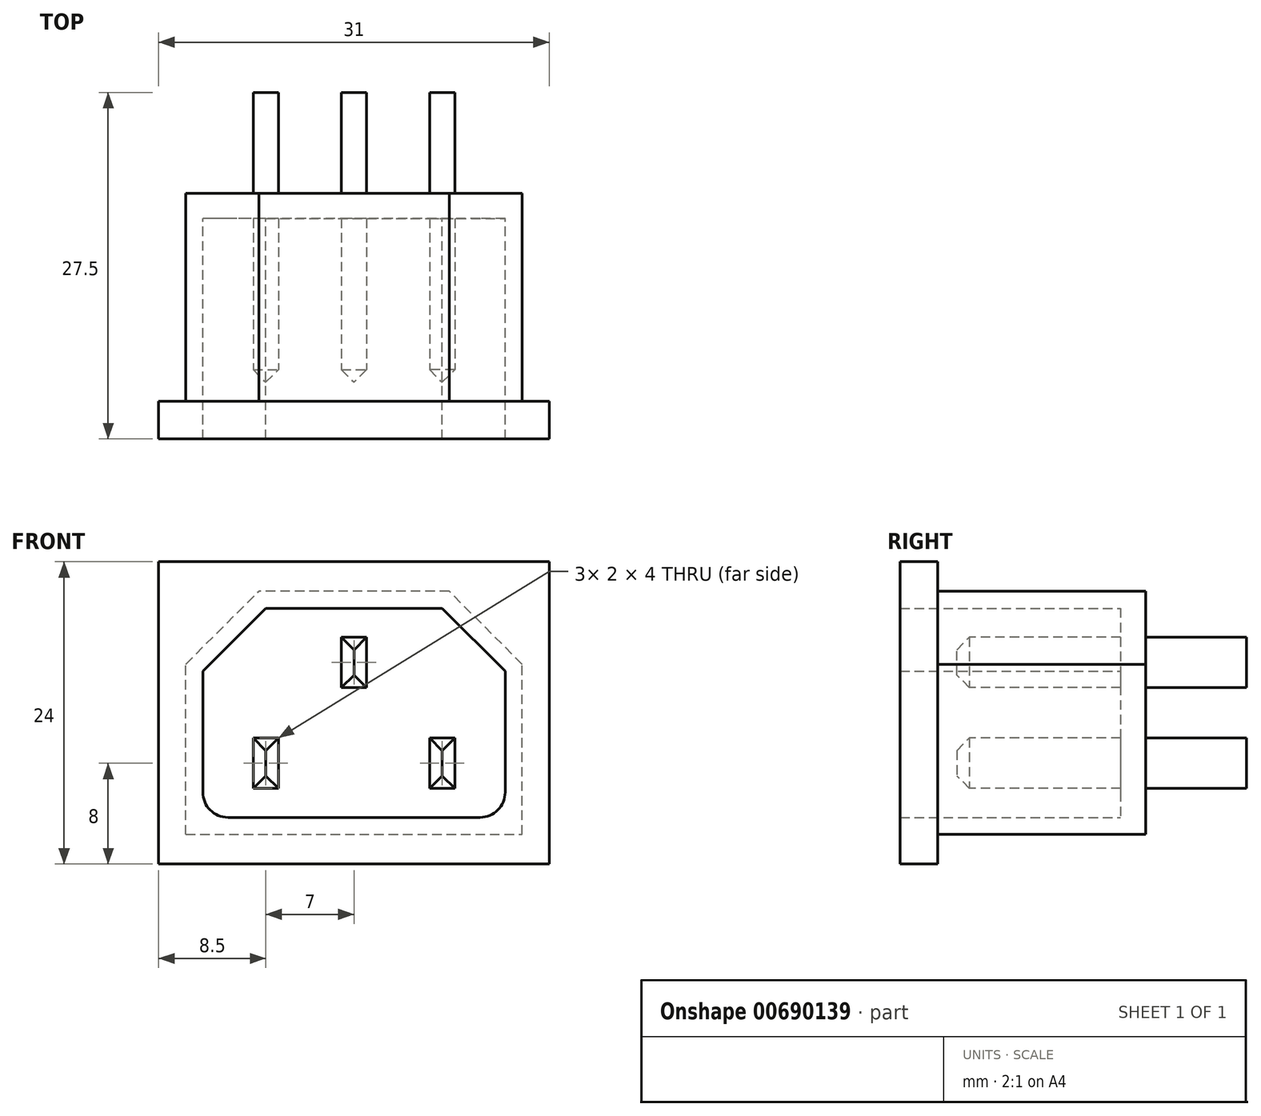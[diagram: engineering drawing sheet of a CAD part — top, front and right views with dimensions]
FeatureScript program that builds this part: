
annotation { "Feature Type Name" : "Feature", "Feature Type Description" : "" }
export const myFeature = defineFeature(function(context is Context, id is Id, definition is map)
    precondition{}
    {
        {
            var Q0;
            Q0=qCreatedBy(makeId("Front.planeOp"),FACE);
            var sketch = newSketch(context, id + "F0", { "sketchPlane" : qUnion([Q0])});
            skLineSegment(sketch, "E0.bottom", {"start": v(15.5, -12) * mm, "end": v(-15.5, -12) * mm});
            skLineSegment(sketch, "E0.top", {"start": v(15.5, 12) * mm, "end": v(-15.5, 12) * mm});
            skLineSegment(sketch, "E0.left", {"start": v(15.5, -12) * mm, "end": v(15.5, 12) * mm});
            skLineSegment(sketch, "E0.right", {"start": v(-15.5, -12) * mm, "end": v(-15.5, 12) * mm});
            skPoint(sketch, "E0.middle", {"position": v(0, 0) * mm});
            skLineSegment(sketch, "E1", {"start": v(-10, -8.3) * mm, "end": v(10, -8.3) * mm});
            skLineSegment(sketch, "E2", {"start": v(12, -6.3) * mm, "end": v(12, 3.3) * mm});
            skLineSegment(sketch, "E3", {"start": v(12, 3.3) * mm, "end": v(7, 8.3) * mm});
            skLineSegment(sketch, "E4", {"start": v(7, 8.3) * mm, "end": v(-7, 8.3) * mm});
            skLineSegment(sketch, "E5.MirrorCS", {"start": v(-12, 3.3) * mm, "end": v(-7, 8.3) * mm});
            skLineSegment(sketch, "E6.MirrorCS", {"start": v(-12, -6.3) * mm, "end": v(-12, 3.3) * mm});
            skPoint(sketch, "E7.visualSharp", {"position": v(-12, -8.3) * mm});
            skArc(sketch, "E7.filletArc", {"start": v(-12, -6.3) * mm, "mid": v(-11.41, -7.71) * mm, "end": v(-10, -8.3) * mm});
            skPoint(sketch, "E8.visualSharp", {"position": v(12, -8.3) * mm});
            skArc(sketch, "E8.filletArc", {"start": v(10, -8.3) * mm, "mid": v(11.41, -7.71) * mm, "end": v(12, -6.3) * mm});
            skSolve(sketch);
        }
        {
            var Q0;
            Q0 = qSketchRegion(id + "F0", true);
            extrude(context, id + "F1", {"entities" : qUnion([Q0]), "depth" : 3 * mm, "offsetDistance" : 25 * mm});
        }
        {
            var Q0;
            Q0=makeQuery(id+"F1.opExtrude","CAP_FACE",FACE,{"disambiguationData":[OSD([sQuery(id+"F0.wireOp",EDGE,"E0.bottom"),sQuery(id+"F0.wireOp",EDGE,"E0.top"),sQuery(id+"F0.wireOp",EDGE,"E0.left"),sQuery(id+"F0.wireOp",EDGE,"E0.right"),sQuery(id+"F0.wireOp",EDGE,"E1"),sQuery(id+"F0.wireOp",EDGE,"E2"),sQuery(id+"F0.wireOp",EDGE,"E3"),sQuery(id+"F0.wireOp",EDGE,"E4"),sQuery(id+"F0.wireOp",EDGE,"E5.MirrorCS"),sQuery(id+"F0.wireOp",EDGE,"E6.MirrorCS"),sQuery(id+"F0.wireOp",EDGE,"E7.filletArc"),sQuery(id+"F0.wireOp",EDGE,"E8.filletArc")])],"isStart":true});
            var sketch = newSketch(context, id + "F2", { "sketchPlane" : qUnion([Q0])});
            skLineSegment(sketch, "E9.0", {"start": v(-12, 3.3) * mm, "end": v(-7, 8.3) * mm});
            skLineSegment(sketch, "E10.0", {"start": v(-7, 8.3) * mm, "end": v(7, 8.3) * mm});
            skLineSegment(sketch, "E11.0", {"start": v(12, -6.3) * mm, "end": v(12, 3.3) * mm});
            skLineSegment(sketch, "E12.0", {"start": v(12, 3.3) * mm, "end": v(7, 8.3) * mm});
            skArc(sketch, "E13.0", {"start": v(12, -6.3) * mm, "mid": v(11.41, -7.71) * mm, "end": v(10, -8.3) * mm});
            skLineSegment(sketch, "E14.0", {"start": v(10, -8.3) * mm, "end": v(-10, -8.3) * mm});
            skArc(sketch, "E15.0", {"start": v(-10, -8.3) * mm, "mid": v(-11.41, -7.71) * mm, "end": v(-12, -6.3) * mm});
            skLineSegment(sketch, "E16.0", {"start": v(-12, -6.3) * mm, "end": v(-12, 3.3) * mm});
            skLineSegment(sketch, "E17.0", {"start": v(-13.35, 3.86) * mm, "end": v(-7.56, 9.65) * mm});
            skLineSegment(sketch, "E17.1", {"start": v(-13.35, -9.65) * mm, "end": v(-13.35, 3.86) * mm});
            skLineSegment(sketch, "E17.2", {"start": v(-7.56, 9.65) * mm, "end": v(7.56, 9.65) * mm});
            skLineSegment(sketch, "E17.4", {"start": v(13.35, 3.86) * mm, "end": v(7.56, 9.65) * mm});
            skLineSegment(sketch, "E17.5", {"start": v(13.35, -9.65) * mm, "end": v(13.35, 3.86) * mm});
            skLineSegment(sketch, "E17.7", {"start": v(13.35, -9.65) * mm, "end": v(-13.35, -9.65) * mm});
            skSolve(sketch);
        }
        {
            var Q0;
            Q0 = qSketchRegion(id + "F2", true);
            extrude(context, id + "F3", {"entities" : qUnion([Q0]), "operationType" : NewBodyOperationType.ADD, "depth" : 16.5 * mm, "offsetDistance" : 25 * mm});
        }
        {
            var Q0;
            Q0=makeQuery(id+"F3.opExtrude","CAP_FACE",FACE,{"disambiguationData":[OSD([sQuery(id+"F2.wireOp",EDGE,"E9.0"),sQuery(id+"F2.wireOp",EDGE,"E10.0"),sQuery(id+"F2.wireOp",EDGE,"E11.0"),sQuery(id+"F2.wireOp",EDGE,"E12.0"),sQuery(id+"F2.wireOp",EDGE,"E13.0"),sQuery(id+"F2.wireOp",EDGE,"E14.0"),sQuery(id+"F2.wireOp",EDGE,"E15.0"),sQuery(id+"F2.wireOp",EDGE,"E16.0"),sQuery(id+"F2.wireOp",EDGE,"E17.0"),sQuery(id+"F2.wireOp",EDGE,"E17.1"),sQuery(id+"F2.wireOp",EDGE,"E17.2"),sQuery(id+"F2.wireOp",EDGE,"E17.4"),sQuery(id+"F2.wireOp",EDGE,"E17.5"),sQuery(id+"F2.wireOp",EDGE,"E17.7")])],"isStart":false});
            var sketch = newSketch(context, id + "F4", { "sketchPlane" : qUnion([Q0])});
            skLineSegment(sketch, "E18.0.0", {"start": v(-7.56, 9.65) * mm, "end": v(-13.35, 3.86) * mm});
            skLineSegment(sketch, "E18.0.1", {"start": v(-13.35, 3.86) * mm, "end": v(-13.35, -9.65) * mm});
            skLineSegment(sketch, "E18.0.2", {"start": v(-13.35, -9.65) * mm, "end": v(13.35, -9.65) * mm});
            skLineSegment(sketch, "E18.0.3", {"start": v(13.35, -9.65) * mm, "end": v(13.35, 3.86) * mm});
            skLineSegment(sketch, "E18.0.4", {"start": v(13.35, 3.86) * mm, "end": v(7.56, 9.65) * mm});
            skLineSegment(sketch, "E18.0.5", {"start": v(7.56, 9.65) * mm, "end": v(-7.56, 9.65) * mm});
            skSolve(sketch);
        }
        {
            var Q0;
            Q0 = qSketchRegion(id + "F4", true);
            extrude(context, id + "F5", {"entities" : qUnion([Q0]), "operationType" : NewBodyOperationType.ADD, "oppositeDirection" : true, "depth" : 2 * mm, "offsetDistance" : 25 * mm});
        }
        {
            var Q0;
            Q0=makeQuery(id+"F5.boolean.opBoolean","MERGE",FACE,{"derivedFrom":[makeQuery(id+"F3.opExtrude","CAP_FACE",FACE,{"disambiguationData":[OSD([sQuery(id+"F2.wireOp",EDGE,"E9.0"),sQuery(id+"F2.wireOp",EDGE,"E10.0"),sQuery(id+"F2.wireOp",EDGE,"E11.0"),sQuery(id+"F2.wireOp",EDGE,"E12.0"),sQuery(id+"F2.wireOp",EDGE,"E13.0"),sQuery(id+"F2.wireOp",EDGE,"E14.0"),sQuery(id+"F2.wireOp",EDGE,"E15.0"),sQuery(id+"F2.wireOp",EDGE,"E16.0"),sQuery(id+"F2.wireOp",EDGE,"E17.0"),sQuery(id+"F2.wireOp",EDGE,"E17.1"),sQuery(id+"F2.wireOp",EDGE,"E17.2"),sQuery(id+"F2.wireOp",EDGE,"E17.4"),sQuery(id+"F2.wireOp",EDGE,"E17.5"),sQuery(id+"F2.wireOp",EDGE,"E17.7")])],"isStart":false}),makeQuery(id+"F5.opExtrude","CAP_FACE",FACE,{"disambiguationData":[OSD([sQuery(id+"F4.wireOp",EDGE,"E18.0.0"),sQuery(id+"F4.wireOp",EDGE,"E18.0.1"),sQuery(id+"F4.wireOp",EDGE,"E18.0.2"),sQuery(id+"F4.wireOp",EDGE,"E18.0.3"),sQuery(id+"F4.wireOp",EDGE,"E18.0.4"),sQuery(id+"F4.wireOp",EDGE,"E18.0.5")])],"isStart":true})]});
            var sketch = newSketch(context, id + "F6", { "sketchPlane" : qUnion([Q0])});
            skLineSegment(sketch, "E19.bottom", {"start": v(1, 2) * mm, "end": v(-1, 2) * mm});
            skLineSegment(sketch, "E19.top", {"start": v(1, 6) * mm, "end": v(-1, 6) * mm});
            skLineSegment(sketch, "E19.left", {"start": v(1, 2) * mm, "end": v(1, 6) * mm});
            skLineSegment(sketch, "E19.right", {"start": v(-1, 2) * mm, "end": v(-1, 6) * mm});
            skPoint(sketch, "E19.middle", {"position": v(0, 4) * mm});
            skLineSegment(sketch, "E20.bottom", {"start": v(8, -6) * mm, "end": v(6, -6) * mm});
            skLineSegment(sketch, "E20.top", {"start": v(8, -2) * mm, "end": v(6, -2) * mm});
            skLineSegment(sketch, "E20.left", {"start": v(8, -6) * mm, "end": v(8, -2) * mm});
            skLineSegment(sketch, "E20.right", {"start": v(6, -6) * mm, "end": v(6, -2) * mm});
            skPoint(sketch, "E20.middle", {"position": v(7, -4) * mm});
            skLineSegment(sketch, "E21.MirrorCS", {"start": v(-8, -6) * mm, "end": v(-8, -2) * mm});
            skLineSegment(sketch, "E22.MirrorCS", {"start": v(-6, -6) * mm, "end": v(-6, -2) * mm});
            skPoint(sketch, "E23.MirrorP", {"position": v(-7, -4) * mm});
            skLineSegment(sketch, "E24.MirrorCS", {"start": v(-8, -2) * mm, "end": v(-6, -2) * mm});
            skLineSegment(sketch, "E25.MirrorCS", {"start": v(-8, -6) * mm, "end": v(-6, -6) * mm});
            skSolve(sketch);
        }
        {
            var Q0;
            Q0 = qSketchRegion(id + "F6", true);
            extrude(context, id + "F7", {"entities" : qUnion([Q0]), "operationType" : NewBodyOperationType.ADD, "depth" : 8 * mm, "offsetDistance" : 25 * mm, "hasSecondDirection" : true, "secondDirectionOppositeDirection" : true, "secondDirectionDepth" : 15 * mm});
        }
        {
            var Q0;
            Q0=makeQuery(id+"F7.opExtrude","CAP_FACE",FACE,{"disambiguationData":[OSD([sQuery(id+"F6.wireOp",EDGE,"E19.bottom"),sQuery(id+"F6.wireOp",EDGE,"E19.top"),sQuery(id+"F6.wireOp",EDGE,"E19.left"),sQuery(id+"F6.wireOp",EDGE,"E19.right")])],"isStart":true});
            var Q1;
            Q1=makeQuery(id+"F7.opExtrude","CAP_FACE",FACE,{"disambiguationData":[OSD([sQuery(id+"F6.wireOp",EDGE,"E21.MirrorCS"),sQuery(id+"F6.wireOp",EDGE,"E22.MirrorCS"),sQuery(id+"F6.wireOp",EDGE,"E24.MirrorCS"),sQuery(id+"F6.wireOp",EDGE,"E25.MirrorCS")])],"isStart":true});
            var Q2;
            Q2=makeQuery(id+"F7.opExtrude","CAP_FACE",FACE,{"disambiguationData":[OSD([sQuery(id+"F6.wireOp",EDGE,"E20.bottom"),sQuery(id+"F6.wireOp",EDGE,"E20.top"),sQuery(id+"F6.wireOp",EDGE,"E20.left"),sQuery(id+"F6.wireOp",EDGE,"E20.right")])],"isStart":true});
            chamfer(context, id + "F8", {"entities" : qUnion([Q0, Q1, Q2]), "width" : 1 * mm, "tangentPropagation" : true});
        }
    });
